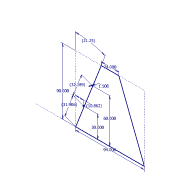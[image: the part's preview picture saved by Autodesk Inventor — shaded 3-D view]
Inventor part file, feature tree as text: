
AUTODESK INVENTOR PART (.ipt)
format: ipt  version: 2012 (Build 160160000, 160)  size: 68,608 bytes
history: native  units: in
note: dims shown in document units (in); Inventor stores cm internally (conversion verified against a paired STEP export)
features: sketch x1
ambient origin geometry x8: Origin, YZ Plane, XZ Plane, XY Plane, X Axis, Y Axis, Z Axis, Center Point
feature tree (1):
  sketch  "Sketch1"  dims[d0=90.0in d1=94.0in d2=24.0in d3=0.146in d4=30.0in d6=60.0in d7=1.5in d10=10.8619in d14=32.1887in d15=31.9058in]
